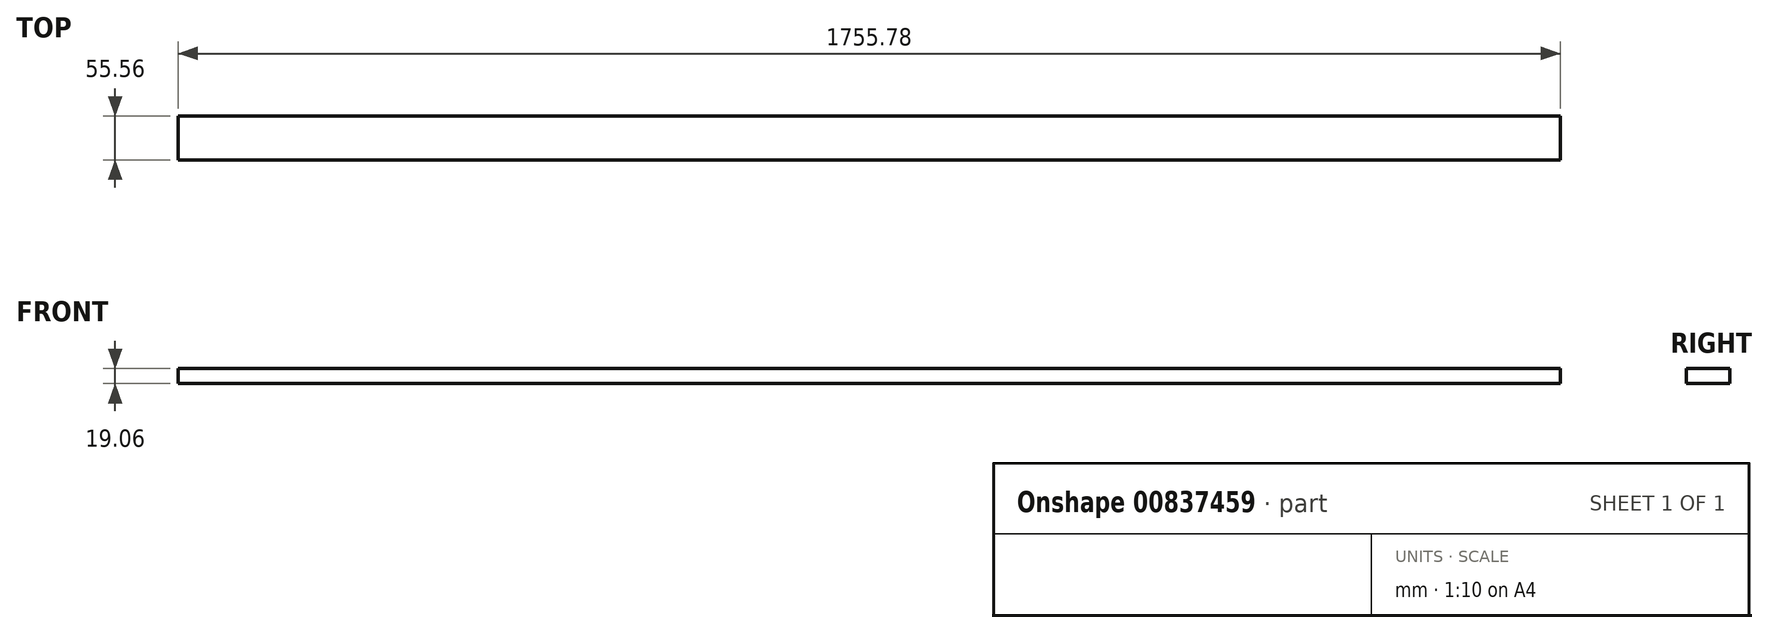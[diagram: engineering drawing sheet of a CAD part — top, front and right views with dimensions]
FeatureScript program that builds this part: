
annotation { "Feature Type Name" : "Feature", "Feature Type Description" : "" }
export const myFeature = defineFeature(function(context is Context, id is Id, definition is map)
    precondition{}
    {
        {
            var Q0;
            Q0=qCreatedBy(makeId("Right.planeOp"),FACE);
            var sketch = newSketch(context, id + "F0", { "sketchPlane" : qUnion([Q0])});
            skLineSegment(sketch, "E0.bottom", {"start": v(27.78, 9.53) * mm, "end": v(-27.78, 9.53) * mm});
            skLineSegment(sketch, "E0.top", {"start": v(27.78, -9.53) * mm, "end": v(-27.78, -9.53) * mm});
            skLineSegment(sketch, "E0.left", {"start": v(27.78, 9.53) * mm, "end": v(27.78, -9.52) * mm});
            skLineSegment(sketch, "E0.right", {"start": v(-27.78, 9.53) * mm, "end": v(-27.78, -9.52) * mm});
            skPoint(sketch, "E0.middle", {"position": v(0, 0) * mm});
            skSolve(sketch);
        }
        {
            var Q0;
            Q0=makeQuery(id+"F0.imprint","IMPRINT",FACE,{"disambiguationData":[TD([[makeQuery(id+"F0.imprint","IMPRINT",EDGE,{"derivedFrom":sQuery(id+"F0.wireOp",EDGE,"E0.bottom")}),1.0]])]});
            extrude(context, id + "F1", {"entities" : qUnion([Q0]), "endBound" : BoundingType.SYMMETRIC, "depth" : 1755.77 * mm, "offsetDistance" : 25.4 * mm});
        }
    });
